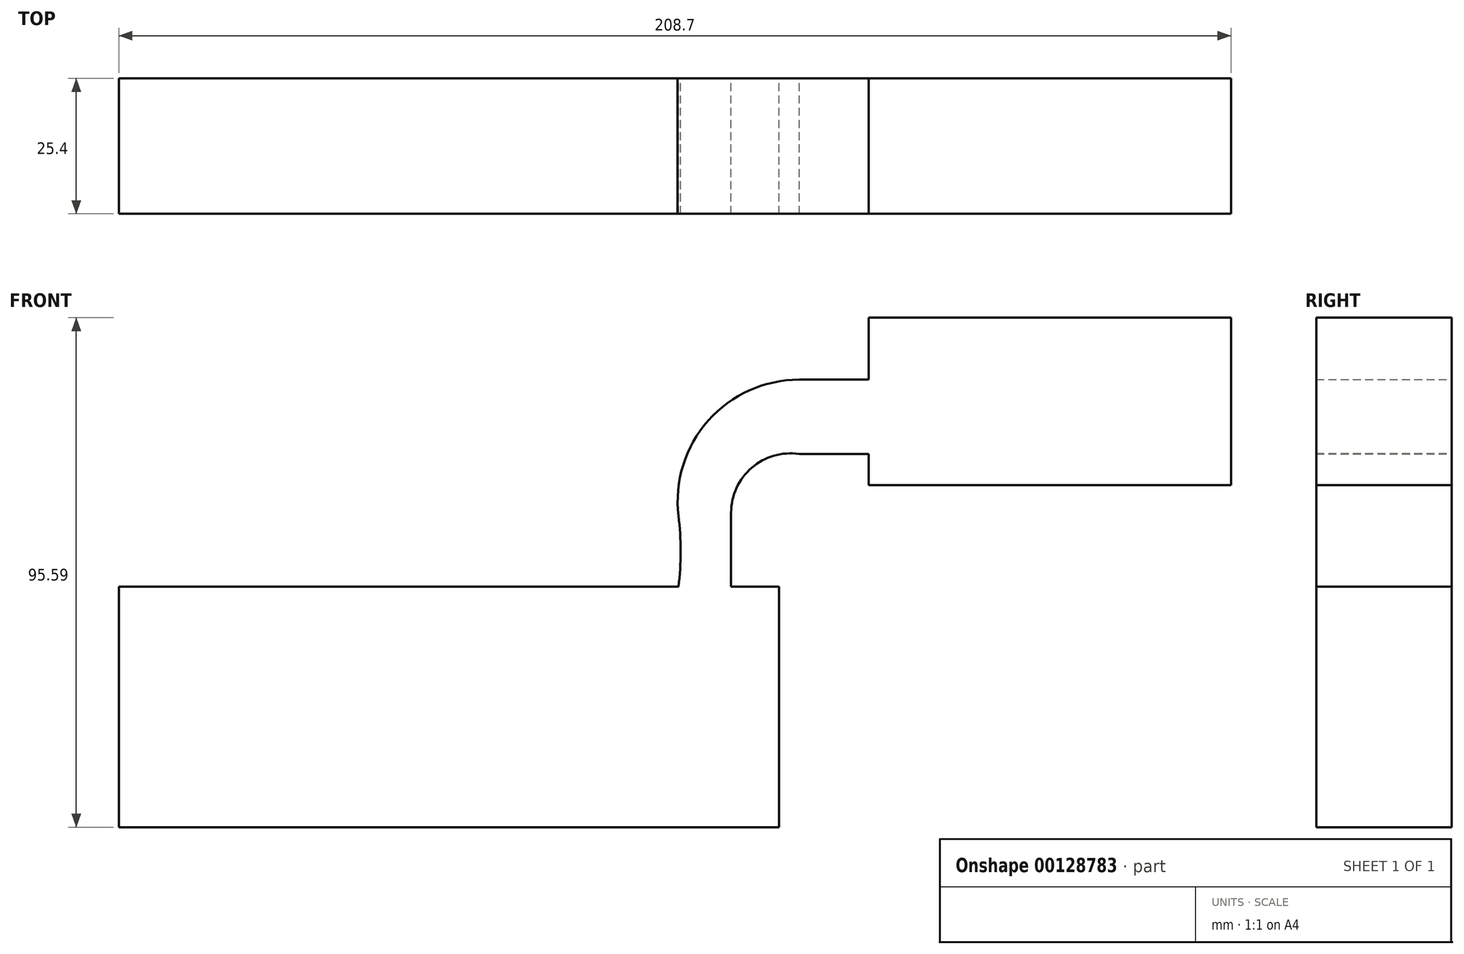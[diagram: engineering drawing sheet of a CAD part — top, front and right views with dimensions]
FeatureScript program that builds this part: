
annotation { "Feature Type Name" : "Feature", "Feature Type Description" : "" }
export const myFeature = defineFeature(function(context is Context, id is Id, definition is map)
    precondition{}
    {
        {
            var Q0;
            Q0=qCreatedBy(makeId("Front.planeOp"),FACE);
            var sketch = newSketch(context, id + "F0", { "sketchPlane" : qUnion([Q0])});
            skLineSegment(sketch, "E0.bottom", {"start": v(-61.96, -22.55) * mm, "end": v(61.96, -22.55) * mm});
            skLineSegment(sketch, "E0.top", {"start": v(-61.96, 22.55) * mm, "end": v(61.96, 22.55) * mm});
            skLineSegment(sketch, "E0.left", {"start": v(-61.96, -22.55) * mm, "end": v(-61.96, 22.55) * mm});
            skLineSegment(sketch, "E0.right", {"start": v(61.96, -22.55) * mm, "end": v(61.96, 22.55) * mm});
            skPoint(sketch, "E0.middle", {"position": v(0, 0) * mm});
            skLineSegment(sketch, "E1.bottom", {"start": v(146.74, 41.65) * mm, "end": v(78.74, 41.65) * mm});
            skLineSegment(sketch, "E1.top", {"start": v(146.74, 73.04) * mm, "end": v(78.74, 73.04) * mm});
            skLineSegment(sketch, "E1.left", {"start": v(146.74, 41.65) * mm, "end": v(146.74, 73.04) * mm});
            skLineSegment(sketch, "E1.right", {"start": v(78.74, 41.65) * mm, "end": v(78.74, 73.04) * mm});
            skPoint(sketch, "E1.middle", {"position": v(112.74, 57.35) * mm});
            skLineSegment(sketch, "E2", {"start": v(52.94, 22.55) * mm, "end": v(52.94, 36.43) * mm});
            skArc(sketch, "E3", {"start": v(52.94, 36.43) * mm, "mid": v(56.8, 44.87) * mm, "end": v(65.72, 47.46) * mm});
            skLineSegment(sketch, "E4", {"start": v(65.72, 47.46) * mm, "end": v(82.85, 47.46) * mm});
            skLineSegment(sketch, "E5", {"start": v(82.85, 61.4) * mm, "end": v(65.72, 61.4) * mm});
            skArc(sketch, "E6", {"start": v(65.72, 61.4) * mm, "mid": v(48.64, 53.72) * mm, "end": v(43.07, 35.85) * mm});
            skArc(sketch, "E7", {"start": v(43.07, 35.85) * mm, "mid": v(43.47, 29.2) * mm, "end": v(43.07, 22.55) * mm});
            skSolve(sketch);
        }
        {
            var Q0;
            Q0 = qSketchRegion(id + "F0", true);
            extrude(context, id + "F1", {"entities" : qUnion([Q0]), "depth" : 25.4 * mm});
        }
    });
